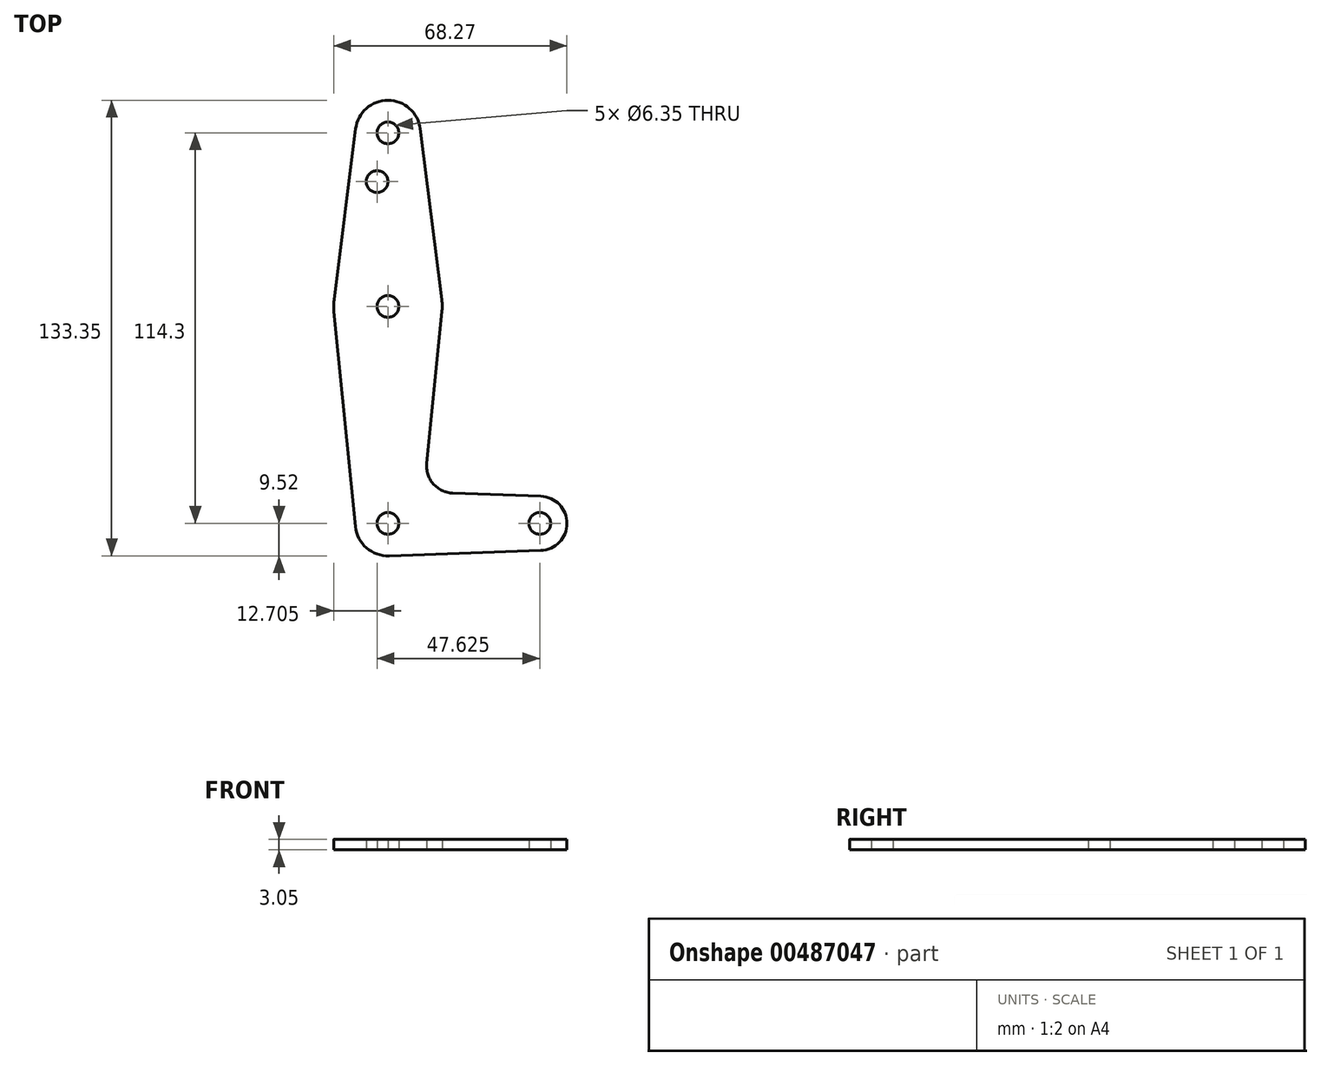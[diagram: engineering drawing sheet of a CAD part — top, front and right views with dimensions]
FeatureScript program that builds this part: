
annotation { "Feature Type Name" : "Feature", "Feature Type Description" : "" }
export const myFeature = defineFeature(function(context is Context, id is Id, definition is map)
    precondition{}
    {
        {
            var Q0;
            Q0=qCreatedBy(makeId("Top.planeOp"),FACE);
            var sketch = newSketch(context, id + "F0", { "sketchPlane" : qUnion([Q0])});
            skLineSegment(sketch, "E0", {"start": v(0, 0) * mm, "end": v(0, 114.3) * mm, "construction": true});
            skLineSegment(sketch, "E1", {"start": v(0, 0) * mm, "end": v(44.45, 0) * mm, "construction": true});
            skCircle(sketch, "E2", {"center": v(0, 0) * mm, "radius": 9.53 * mm});
            skCircle(sketch, "E3", {"center": v(0, 114.3) * mm, "radius": 9.53 * mm});
            skCircle(sketch, "E4", {"center": v(44.45, 0) * mm, "radius": 7.94 * mm});
            skCircle(sketch, "E5", {"center": v(0, 63.5) * mm, "radius": 15.88 * mm});
            skLineSegment(sketch, "E6", {"start": v(9.45, 115.5) * mm, "end": v(15.75, 65.48) * mm});
            skLineSegment(sketch, "E7", {"start": v(-9.45, 115.5) * mm, "end": v(-15.75, 65.48) * mm});
            skLineSegment(sketch, "E8", {"start": v(15.8, 61.91) * mm, "end": v(11.34, 17.6) * mm});
            skLineSegment(sketch, "E9", {"start": v(-15.8, 61.91) * mm, "end": v(-9.48, -0.95) * mm});
            skLineSegment(sketch, "E10", {"start": v(44.73, 7.93) * mm, "end": v(18.97, 8.85) * mm});
            skLineSegment(sketch, "E11", {"start": v(44.73, -7.93) * mm, "end": v(0.34, -9.52) * mm});
            skCircle(sketch, "E12", {"center": v(0, 114.3) * mm, "radius": 3.18 * mm});
            skCircle(sketch, "E13", {"center": v(-3.18, 100.03) * mm, "radius": 3.18 * mm});
            skCircle(sketch, "E14", {"center": v(0, 63.5) * mm, "radius": 3.18 * mm});
            skCircle(sketch, "E15", {"center": v(0, 0) * mm, "radius": 3.18 * mm});
            skCircle(sketch, "E16", {"center": v(44.45, 0) * mm, "radius": 3.18 * mm});
            skArc(sketch, "E17.filletArc", {"start": v(11.34, 17.6) * mm, "mid": v(13.26, 11.57) * mm, "end": v(18.97, 8.85) * mm});
            skSolve(sketch);
        }
        {
            var Q0;
            {var subQ0=sQuery(id+"F0.wireOp",EDGE,"E6");Q0=makeQuery(id+"F0.imprint","IMPRINT",FACE,{"disambiguationData":[TD([[makeQuery(id+"F0.imprint","IMPRINT",EDGE,{"derivedFrom":subQ0}),-1.0]])]});}
            var Q1;
            Q1=makeQuery(id+"F0.imprint","IMPRINT",FACE,{"disambiguationData":[TD([[makeQuery(id+"F0.imprint","IMPRINT",EDGE,{"derivedFrom":sQuery(id+"F0.wireOp",EDGE,"E12")}),-1.0]])]});
            var Q2;
            Q2=makeQuery(id+"F0.imprint","IMPRINT",FACE,{"disambiguationData":[TD([[makeQuery(id+"F0.imprint","IMPRINT",EDGE,{"derivedFrom":sQuery(id+"F0.wireOp",EDGE,"E14")}),-1.0]])]});
            var Q3;
            {var subQ0=sQuery(id+"F0.wireOp",EDGE,"E8");Q3=makeQuery(id+"F0.imprint","IMPRINT",FACE,{"disambiguationData":[TD([[makeQuery(id+"F0.imprint","IMPRINT",EDGE,{"derivedFrom":subQ0}),-1.0]])]});}
            var Q4;
            Q4=makeQuery(id+"F0.imprint","IMPRINT",FACE,{"disambiguationData":[TD([[makeQuery(id+"F0.imprint","IMPRINT",EDGE,{"derivedFrom":sQuery(id+"F0.wireOp",EDGE,"E15")}),-1.0]])]});
            var Q5;
            Q5=makeQuery(id+"F0.imprint","IMPRINT",FACE,{"disambiguationData":[TD([[makeQuery(id+"F0.imprint","IMPRINT",EDGE,{"derivedFrom":sQuery(id+"F0.wireOp",EDGE,"E16")}),-1.0]])]});
            extrude(context, id + "F1", {"entities" : qUnion([Q0, Q1, Q2, Q3, Q4, Q5]), "depth" : 3.05 * mm});
        }
    });
